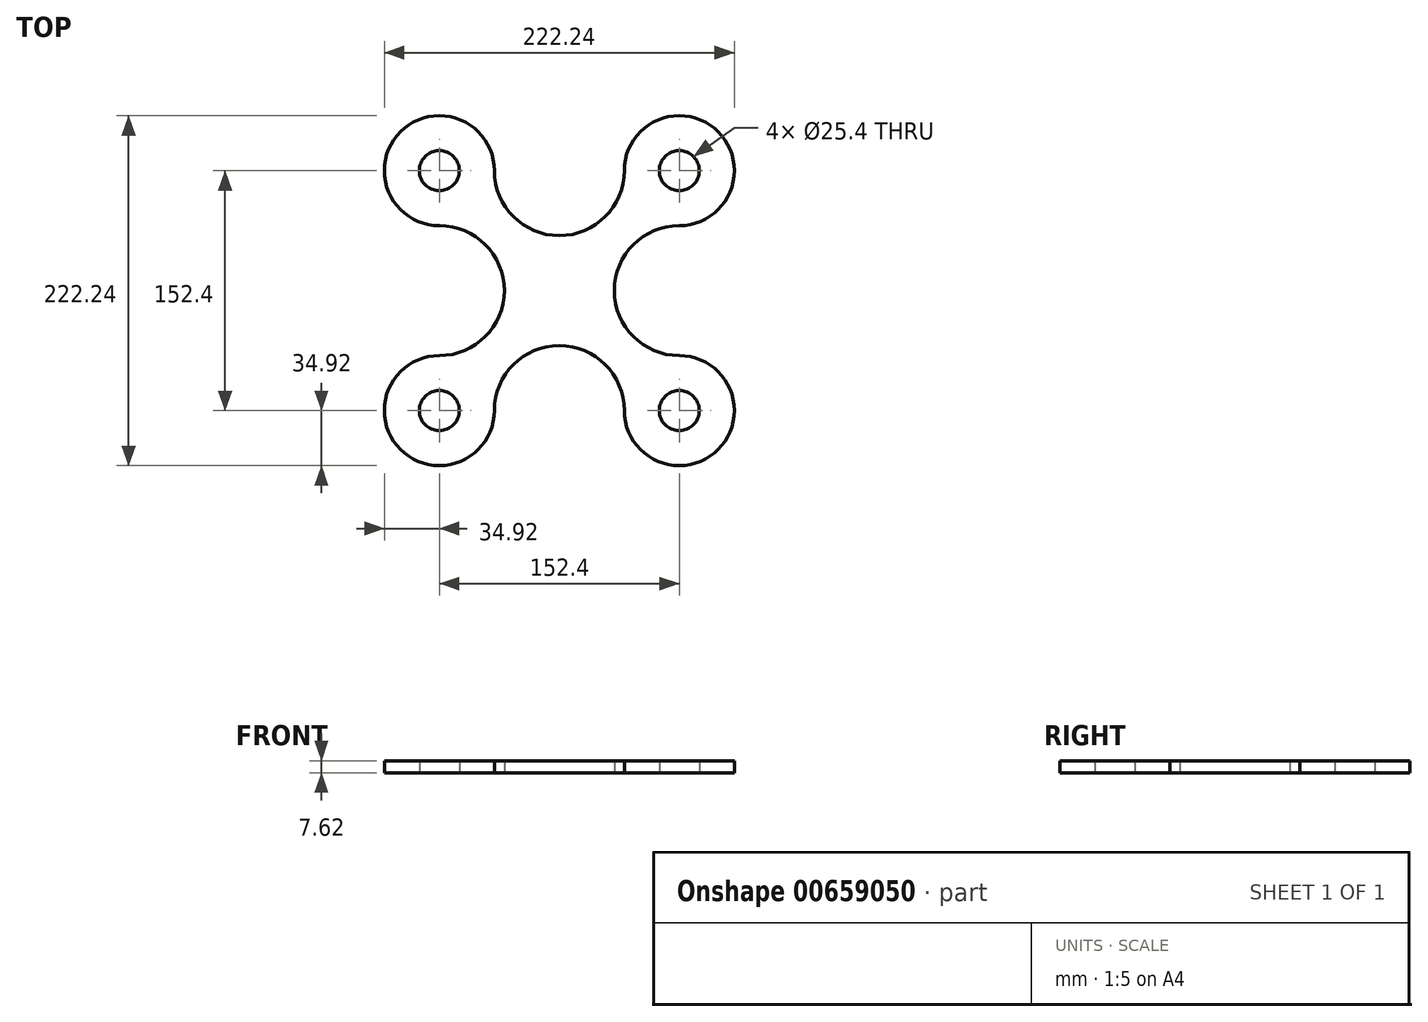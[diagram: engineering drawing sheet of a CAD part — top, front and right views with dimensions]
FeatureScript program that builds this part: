
annotation { "Feature Type Name" : "Feature", "Feature Type Description" : "" }
export const myFeature = defineFeature(function(context is Context, id is Id, definition is map)
    precondition{}
    {
        {
            var Q0;
            Q0=qCreatedBy(makeId("Top.planeOp"),FACE);
            var sketch = newSketch(context, id + "F0", { "sketchPlane" : qUnion([Q0])});
            skPoint(sketch, "E0.middle", {"position": v(0, 0) * mm});
            skArc(sketch, "E1", {"start": v(-41.28, 76.2) * mm, "mid": v(0, 34.93) * mm, "end": v(41.28, 76.2) * mm});
            skArc(sketch, "E2", {"start": v(-76.2, -41.28) * mm, "mid": v(-34.92, 0) * mm, "end": v(-76.2, 41.28) * mm});
            skArc(sketch, "E3", {"start": v(41.28, -76.2) * mm, "mid": v(0, -34.93) * mm, "end": v(-41.27, -76.2) * mm});
            skArc(sketch, "E4", {"start": v(76.2, 41.28) * mm, "mid": v(34.92, 0) * mm, "end": v(76.2, -41.28) * mm});
            skArc(sketch, "E5", {"start": v(-41.27, 76.2) * mm, "mid": v(-100.9, 100.9) * mm, "end": v(-76.2, 41.28) * mm});
            skArc(sketch, "E6", {"start": v(76.2, 41.28) * mm, "mid": v(100.9, 100.9) * mm, "end": v(41.27, 76.2) * mm});
            skArc(sketch, "E7", {"start": v(-76.2, -41.28) * mm, "mid": v(-100.9, -100.9) * mm, "end": v(-41.27, -76.2) * mm});
            skArc(sketch, "E8", {"start": v(41.28, -76.2) * mm, "mid": v(100.9, -100.9) * mm, "end": v(76.2, -41.28) * mm});
            skSolve(sketch);
        }
        {
            var Q0;
            Q0 = qSketchRegion(id + "F0", true);
            extrude(context, id + "F1", {"entities" : qUnion([Q0]), "depth" : 7.62 * mm, "offsetDistance" : 25.4 * mm});
        }
        {
            var Q0;
            Q0=qCreatedBy(makeId("Top.planeOp"),FACE);
            var sketch = newSketch(context, id + "F2", { "sketchPlane" : qUnion([Q0])});
            skPoint(sketch, "E9", {"position": v(-76.2, 76.2) * mm});
            skSolve(sketch);
        }
        {
            var Q0;
            Q0=sQuery(id+"F2.wireOp",VERTEX,"E9");
            var Q1;
            Q1=makeQuery(id+"F1.opExtrude","SWEPT_BODY",BODY,{"disambiguationData":[OSD([sQuery(id+"F0.wireOp",EDGE,"E1"),sQuery(id+"F0.wireOp",EDGE,"E2"),sQuery(id+"F0.wireOp",EDGE,"E3"),sQuery(id+"F0.wireOp",EDGE,"E4"),sQuery(id+"F0.wireOp",EDGE,"E5"),sQuery(id+"F0.wireOp",EDGE,"E6"),sQuery(id+"F0.wireOp",EDGE,"E7"),sQuery(id+"F0.wireOp",EDGE,"E8")])]});
            hole(context, id + "F3", {"style" : HoleStyle.SIMPLE, "endStyle" : HoleEndStyle.THROUGH, "oppositeDirection" : true, "holeDiameter" : 25.4 * mm, "majorDiameter" : 6.35 * mm, "isTappedThrough" : true, "tappedDepth" : 12.7 * mm, "tapClearance" : 3, "locations" : qUnion([Q0]), "scope" : qUnion([Q1])});
        }
        {
            var Q0;
            Q0=qCreatedBy(makeId("Top.planeOp"),FACE);
            var sketch = newSketch(context, id + "F4", { "sketchPlane" : qUnion([Q0])});
            skPoint(sketch, "E10", {"position": v(-76.2, -76.2) * mm});
            skPoint(sketch, "E11", {"position": v(76.2, -76.2) * mm});
            skPoint(sketch, "E12", {"position": v(76.2, 76.2) * mm});
            skSolve(sketch);
        }
        {
            var Q0;
            Q0=sQuery(id+"F4.wireOp",VERTEX,"E10");
            var Q1;
            Q1=sQuery(id+"F4.wireOp",VERTEX,"E11");
            var Q2;
            Q2=sQuery(id+"F4.wireOp",VERTEX,"E12");
            var Q3;
            Q3=makeQuery(id+"F1.opExtrude","SWEPT_BODY",BODY,{"disambiguationData":[OSD([sQuery(id+"F0.wireOp",EDGE,"E1"),sQuery(id+"F0.wireOp",EDGE,"E2"),sQuery(id+"F0.wireOp",EDGE,"E3"),sQuery(id+"F0.wireOp",EDGE,"E4"),sQuery(id+"F0.wireOp",EDGE,"E5"),sQuery(id+"F0.wireOp",EDGE,"E6"),sQuery(id+"F0.wireOp",EDGE,"E7"),sQuery(id+"F0.wireOp",EDGE,"E8")])]});
            hole(context, id + "F5", {"style" : HoleStyle.SIMPLE, "endStyle" : HoleEndStyle.THROUGH, "oppositeDirection" : true, "holeDiameter" : 25.4 * mm, "majorDiameter" : 6.35 * mm, "isTappedThrough" : true, "tappedDepth" : 12.7 * mm, "tapClearance" : 3, "locations" : qUnion([Q0, Q1, Q2]), "scope" : qUnion([Q3])});
        }
    });
